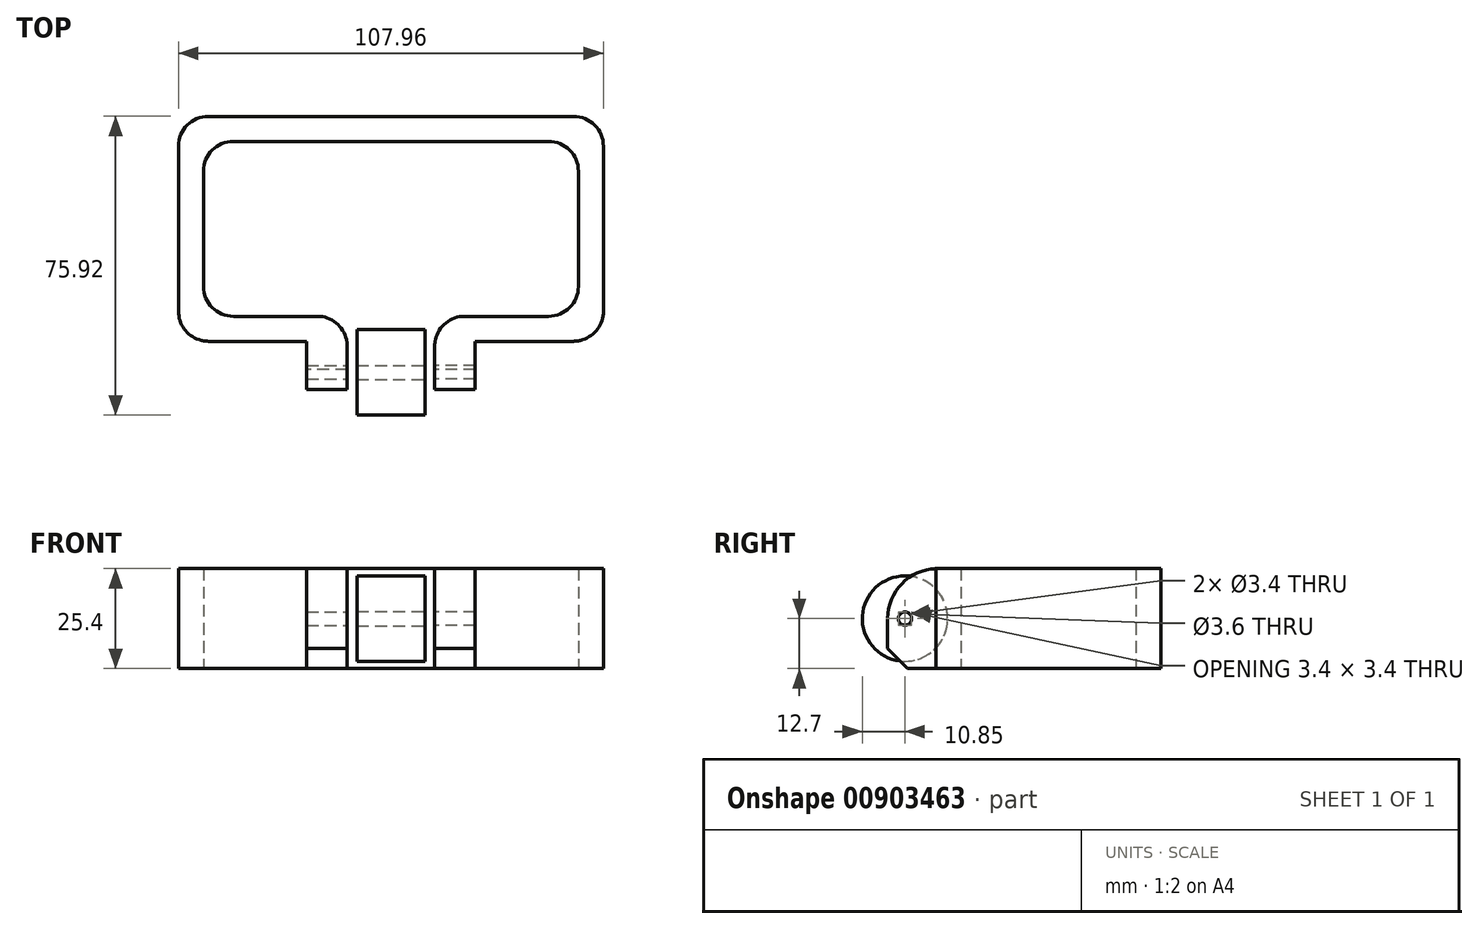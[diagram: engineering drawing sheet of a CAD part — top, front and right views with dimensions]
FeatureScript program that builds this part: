
annotation { "Feature Type Name" : "Feature", "Feature Type Description" : "" }
export const myFeature = defineFeature(function(context is Context, id is Id, definition is map)
    precondition{}
    {
        {
            var Q0;
            Q0=qCreatedBy(makeId("Top.planeOp"),FACE);
            var sketch = newSketch(context, id + "F0", { "sketchPlane" : qUnion([Q0])});
            skLineSegment(sketch, "E0.bottom", {"start": v(53.98, -28.57) * mm, "end": v(-53.98, -28.58) * mm});
            skLineSegment(sketch, "E0.top", {"start": v(53.98, 28.58) * mm, "end": v(-53.98, 28.57) * mm});
            skLineSegment(sketch, "E0.left", {"start": v(53.98, -28.58) * mm, "end": v(53.98, 28.57) * mm});
            skLineSegment(sketch, "E0.right", {"start": v(-53.98, -28.57) * mm, "end": v(-53.98, 28.58) * mm});
            skPoint(sketch, "E0.middle", {"position": v(0, 0) * mm});
            skLineSegment(sketch, "E1.bottom", {"start": v(47.63, -22.22) * mm, "end": v(-47.63, -22.23) * mm});
            skLineSegment(sketch, "E1.top", {"start": v(47.63, 22.23) * mm, "end": v(-47.63, 22.23) * mm});
            skLineSegment(sketch, "E1.left", {"start": v(47.63, -22.23) * mm, "end": v(47.63, 22.23) * mm});
            skLineSegment(sketch, "E1.right", {"start": v(-47.63, -22.23) * mm, "end": v(-47.63, 22.22) * mm});
            skLineSegment(sketch, "E2", {"start": v(0, 14) * mm, "end": v(0, -15.5) * mm, "construction": true});
            skPoint(sketch, "E2.startSnap0", {"position": v(0, 22.23) * mm});
            skLineSegment(sketch, "E3.bottom", {"start": v(8.63, -47.34) * mm, "end": v(-8.63, -47.34) * mm});
            skLineSegment(sketch, "E3.top", {"start": v(8.63, -25.64) * mm, "end": v(-8.63, -25.64) * mm});
            skLineSegment(sketch, "E3.left", {"start": v(8.63, -47.34) * mm, "end": v(8.63, -25.64) * mm});
            skLineSegment(sketch, "E3.right", {"start": v(-8.63, -47.34) * mm, "end": v(-8.63, -25.64) * mm});
            skPoint(sketch, "E3.middle", {"position": v(0, -36.49) * mm});
            skLineSegment(sketch, "E4.bottom", {"start": v(-21.42, -28.58) * mm, "end": v(-11.11, -28.58) * mm});
            skLineSegment(sketch, "E4.top", {"start": v(-21.42, -40.9) * mm, "end": v(-11.11, -40.9) * mm});
            skLineSegment(sketch, "E4.left", {"start": v(-21.42, -28.58) * mm, "end": v(-21.42, -40.9) * mm});
            skLineSegment(sketch, "E4.right", {"start": v(-11.11, -28.58) * mm, "end": v(-11.11, -40.9) * mm});
            skLineSegment(sketch, "E5", {"start": v(-11.11, -28.58) * mm, "end": v(-11.11, -22.23) * mm});
            skLineSegment(sketch, "E6.MirrorCS", {"start": v(11.11, -28.58) * mm, "end": v(11.11, -22.23) * mm});
            skLineSegment(sketch, "E7.MirrorCS", {"start": v(11.11, -28.58) * mm, "end": v(11.11, -40.9) * mm});
            skLineSegment(sketch, "E8.MirrorCS", {"start": v(21.42, -40.9) * mm, "end": v(11.11, -40.9) * mm});
            skLineSegment(sketch, "E9.MirrorCS", {"start": v(21.42, -28.58) * mm, "end": v(21.42, -40.9) * mm});
            skLineSegment(sketch, "E10", {"start": v(-8.63, -36.49) * mm, "end": v(8.63, -36.49) * mm});
            skSolve(sketch);
        }
        {
            var Q0;
            Q0=makeQuery(id+"F0.imprint","IMPRINT",FACE,{"disambiguationData":[TD([[makeQuery(id+"F0.imprint","IMPRINT",EDGE,{"derivedFrom":sQuery(id+"F0.wireOp",EDGE,"E0.top")}),1.0]])]});
            var Q1;
            Q1=makeQuery(id+"F0.imprint","IMPRINT",FACE,{"disambiguationData":[TD([[makeQuery(id+"F0.imprint","IMPRINT",EDGE,{"derivedFrom":sQuery(id+"F0.wireOp",EDGE,"E4.top")}),1.0]])]});
            var Q2;
            {var subQ0=sQuery(id+"F0.wireOp",EDGE,"E7.MirrorCS");Q2=makeQuery(id+"F0.imprint","IMPRINT",FACE,{"disambiguationData":[TD([[makeQuery(id+"F0.imprint","IMPRINT",EDGE,{"derivedFrom":subQ0}),1.0]])]});}
            extrude(context, id + "F1", {"entities" : qUnion([Q0, Q1, Q2]), "depth" : 25.4 * mm, "offsetDistance" : 25.4 * mm});
        }
        {
            var Q0;
            {var subQ0=sQuery(id+"F0.wireOp",EDGE,"E3.bottom");Q0=makeQuery(id+"F0.imprint","IMPRINT",FACE,{"disambiguationData":[TD([[makeQuery(id+"F0.imprint","IMPRINT",EDGE,{"derivedFrom":subQ0}),-1.0]])]});}
            var Q1;
            Q1=sQuery(id+"F0.wireOp",EDGE,"E10");
            revolve(context, id + "F2", {"surfaceOperationType" : NewSurfaceOperationType.NEW, "entities" : qUnion([Q0]), "axis" : qUnion([Q1]), "revolveType" : RevolveType.FULL});
        }
        {
            var Q0;
            Q0=makeQuery(id+"F2.opRevolve","SWEPT_BODY",BODY,{"disambiguationData":[OSD([sQuery(id+"F0.wireOp",EDGE,"E3.bottom"),sQuery(id+"F0.wireOp",EDGE,"E3.left"),sQuery(id+"F0.wireOp",EDGE,"E3.right"),sQuery(id+"F0.wireOp",EDGE,"E10")])]});
            transform(context, id + "F3", {"entities" : qUnion([Q0]), "transformType" : TransformType.TRANSLATION_3D, "dx" : 0 * mm, "dy" : 0 * mm, "dz" : 12.7 * mm, "makeCopy" : false});
        }
        {
            var Q0;
            Q0=makeQuery(id+"F2.opRevolve","SWEPT_FACE",FACE,{"disambiguationData":[OSD([sQuery(id+"F0.wireOp",EDGE,"E3.left")])]});
            var sketch = newSketch(context, id + "F4", { "sketchPlane" : qUnion([Q0])});
            skPoint(sketch, "E11", {"position": v(-36.49, 12.7) * mm});
            skSolve(sketch);
        }
        {
            var Q0;
            Q0=sQuery(id+"F4.wireOp",VERTEX,"E11");
            var Q1;
            Q1=makeQuery(id+"F2.opRevolve","SWEPT_BODY",BODY,{"disambiguationData":[OSD([sQuery(id+"F0.wireOp",EDGE,"E3.bottom"),sQuery(id+"F0.wireOp",EDGE,"E3.left"),sQuery(id+"F0.wireOp",EDGE,"E3.right"),sQuery(id+"F0.wireOp",EDGE,"E10")])]});
            hole(context, id + "F5", {"style" : HoleStyle.SIMPLE, "endStyle" : HoleEndStyle.THROUGH, "holeDiameter" : 3.6 * mm, "majorDiameter" : 6.35 * mm, "isTappedThrough" : true, "tappedDepth" : 12.7 * mm, "tapClearance" : 3, "startFromSketch" : true, "locations" : qUnion([Q0]), "scope" : qUnion([Q1])});
        }
        {
            var Q0;
            Q0=sQuery(id+"F4.wireOp",VERTEX,"E11");
            var Q1;
            Q1=makeQuery(id+"F1.opExtrude","SWEPT_BODY",BODY,{"disambiguationData":[OSD([sQuery(id+"F0.wireOp",EDGE,"E0.bottom"),sQuery(id+"F0.wireOp",EDGE,"E0.top"),sQuery(id+"F0.wireOp",EDGE,"E0.left"),sQuery(id+"F0.wireOp",EDGE,"E0.right"),sQuery(id+"F0.wireOp",EDGE,"E1.bottom"),sQuery(id+"F0.wireOp",EDGE,"E1.top"),sQuery(id+"F0.wireOp",EDGE,"E1.left"),sQuery(id+"F0.wireOp",EDGE,"E1.right"),sQuery(id+"F0.wireOp",EDGE,"E4.top"),sQuery(id+"F0.wireOp",EDGE,"E4.left"),sQuery(id+"F0.wireOp",EDGE,"E4.right"),sQuery(id+"F0.wireOp",EDGE,"E5"),sQuery(id+"F0.wireOp",EDGE,"E6.MirrorCS"),sQuery(id+"F0.wireOp",EDGE,"E7.MirrorCS"),sQuery(id+"F0.wireOp",EDGE,"E8.MirrorCS"),sQuery(id+"F0.wireOp",EDGE,"E9.MirrorCS")])]});
            hole(context, id + "F6", {"style" : HoleStyle.SIMPLE, "endStyle" : HoleEndStyle.THROUGH, "standardTappedOrClearance" : lookupTablePath({ "fit" : "Normal", "standard" : "ISO", "size" : "M3", "type" : "Clearance" }), "standardBlindInLast" : lookupTablePath({ "fit" : "Normal", "standard" : "ISO", "size" : "M3", "type" : "Clearance" }), "holeDiameter" : 3.4 * mm, "majorDiameter" : 6.35 * mm, "isTappedThrough" : true, "tappedDepth" : 12.7 * mm, "tapClearance" : 3, "startFromSketch" : true, "locations" : qUnion([Q0]), "scope" : qUnion([Q1])});
        }
        {
            var Q0;
            Q0=sQuery(id+"F4.wireOp",VERTEX,"E11");
            var Q1;
            Q1=makeQuery(id+"F1.opExtrude","SWEPT_BODY",BODY,{"disambiguationData":[OSD([sQuery(id+"F0.wireOp",EDGE,"E0.bottom"),sQuery(id+"F0.wireOp",EDGE,"E0.top"),sQuery(id+"F0.wireOp",EDGE,"E0.left"),sQuery(id+"F0.wireOp",EDGE,"E0.right"),sQuery(id+"F0.wireOp",EDGE,"E1.bottom"),sQuery(id+"F0.wireOp",EDGE,"E1.top"),sQuery(id+"F0.wireOp",EDGE,"E1.left"),sQuery(id+"F0.wireOp",EDGE,"E1.right"),sQuery(id+"F0.wireOp",EDGE,"E4.top"),sQuery(id+"F0.wireOp",EDGE,"E4.left"),sQuery(id+"F0.wireOp",EDGE,"E4.right"),sQuery(id+"F0.wireOp",EDGE,"E5"),sQuery(id+"F0.wireOp",EDGE,"E6.MirrorCS"),sQuery(id+"F0.wireOp",EDGE,"E7.MirrorCS"),sQuery(id+"F0.wireOp",EDGE,"E8.MirrorCS"),sQuery(id+"F0.wireOp",EDGE,"E9.MirrorCS")])]});
            hole(context, id + "F7", {"style" : HoleStyle.SIMPLE, "endStyle" : HoleEndStyle.THROUGH, "oppositeDirection" : true, "standardTappedOrClearance" : lookupTablePath({ "fit" : "Normal", "standard" : "ISO", "size" : "M3", "type" : "Clearance" }), "standardBlindInLast" : lookupTablePath({ "fit" : "Normal", "standard" : "ISO", "size" : "M3", "type" : "Clearance" }), "holeDiameter" : 3.4 * mm, "majorDiameter" : 6.35 * mm, "isTappedThrough" : true, "tappedDepth" : 12.7 * mm, "tapClearance" : 3, "startFromSketch" : true, "locations" : qUnion([Q0]), "scope" : qUnion([Q1])});
        }
        {
            var Q0;
            Q0=makeQuery(id+"F1.opExtrude","CAP_EDGE",EDGE,{"disambiguationData":[OSD([sQuery(id+"F0.wireOp",EDGE,"E8.MirrorCS")])],"isStart":false});
            var Q1;
            Q1=makeQuery(id+"F1.opExtrude","CAP_EDGE",EDGE,{"disambiguationData":[OSD([sQuery(id+"F0.wireOp",EDGE,"E4.top")])],"isStart":false});
            fillet(context, id + "F8", {"entities" : qUnion([Q0, Q1]), "radius" : 12.7 * mm, "tangentPropagation" : true, "allowEdgeOverflow" : false});
        }
        {
            var Q0;
            Q0=makeQuery(id+"F1.opExtrude","SWEPT_EDGE",EDGE,{"disambiguationData":[OSD([sQuery(id+"F0.wireOp",EDGE,"E0.bottom"),sQuery(id+"F0.wireOp",EDGE,"E0.right")])]});
            var Q1;
            Q1=makeQuery(id+"F1.opExtrude","SWEPT_EDGE",EDGE,{"disambiguationData":[OSD([sQuery(id+"F0.wireOp",EDGE,"E0.top"),sQuery(id+"F0.wireOp",EDGE,"E0.right")])]});
            var Q2;
            Q2=makeQuery(id+"F1.opExtrude","SWEPT_EDGE",EDGE,{"disambiguationData":[OSD([sQuery(id+"F0.wireOp",EDGE,"E1.top"),sQuery(id+"F0.wireOp",EDGE,"E1.left")])]});
            var Q3;
            Q3=makeQuery(id+"F1.opExtrude","SWEPT_EDGE",EDGE,{"disambiguationData":[OSD([sQuery(id+"F0.wireOp",EDGE,"E0.top"),sQuery(id+"F0.wireOp",EDGE,"E0.left")])]});
            var Q4;
            Q4=makeQuery(id+"F1.opExtrude","SWEPT_EDGE",EDGE,{"disambiguationData":[OSD([sQuery(id+"F0.wireOp",EDGE,"E0.bottom"),sQuery(id+"F0.wireOp",EDGE,"E0.left")])]});
            var Q5;
            Q5=makeQuery(id+"F1.opExtrude","SWEPT_EDGE",EDGE,{"disambiguationData":[OSD([sQuery(id+"F0.wireOp",EDGE,"E1.bottom"),sQuery(id+"F0.wireOp",EDGE,"E1.left")])]});
            var Q6;
            Q6=makeQuery(id+"F1.opExtrude","SWEPT_EDGE",EDGE,{"disambiguationData":[OSD([sQuery(id+"F0.wireOp",EDGE,"E1.bottom"),sQuery(id+"F0.wireOp",EDGE,"E1.right")])]});
            var Q7;
            Q7=makeQuery(id+"F1.opExtrude","SWEPT_EDGE",EDGE,{"disambiguationData":[OSD([sQuery(id+"F0.wireOp",EDGE,"E1.top"),sQuery(id+"F0.wireOp",EDGE,"E1.right")])]});
            var Q8;
            Q8=makeQuery(id+"F1.opExtrude","SWEPT_EDGE",EDGE,{"disambiguationData":[OSD([sQuery(id+"F0.wireOp",EDGE,"E1.bottom"),sQuery(id+"F0.wireOp",EDGE,"E5")])]});
            var Q9;
            Q9=makeQuery(id+"F1.opExtrude","SWEPT_EDGE",EDGE,{"disambiguationData":[OSD([sQuery(id+"F0.wireOp",EDGE,"E1.bottom"),sQuery(id+"F0.wireOp",EDGE,"E6.MirrorCS")])]});
            fillet(context, id + "F9", {"entities" : qUnion([Q0, Q1, Q2, Q3, Q4, Q5, Q6, Q7, Q8, Q9]), "radius" : 7.62 * mm, "tangentPropagation" : true, "allowEdgeOverflow" : false});
        }
        {
            var Q0;
            Q0=makeQuery(id+"F1.opExtrude","CAP_EDGE",EDGE,{"disambiguationData":[OSD([sQuery(id+"F0.wireOp",EDGE,"E4.top")])],"isStart":true});
            var Q1;
            Q1=makeQuery(id+"F1.opExtrude","CAP_EDGE",EDGE,{"disambiguationData":[OSD([sQuery(id+"F0.wireOp",EDGE,"E8.MirrorCS")])],"isStart":true});
            chamfer(context, id + "F10", {"entities" : qUnion([Q0, Q1]), "width" : 5.08 * mm, "tangentPropagation" : true});
        }
    });
